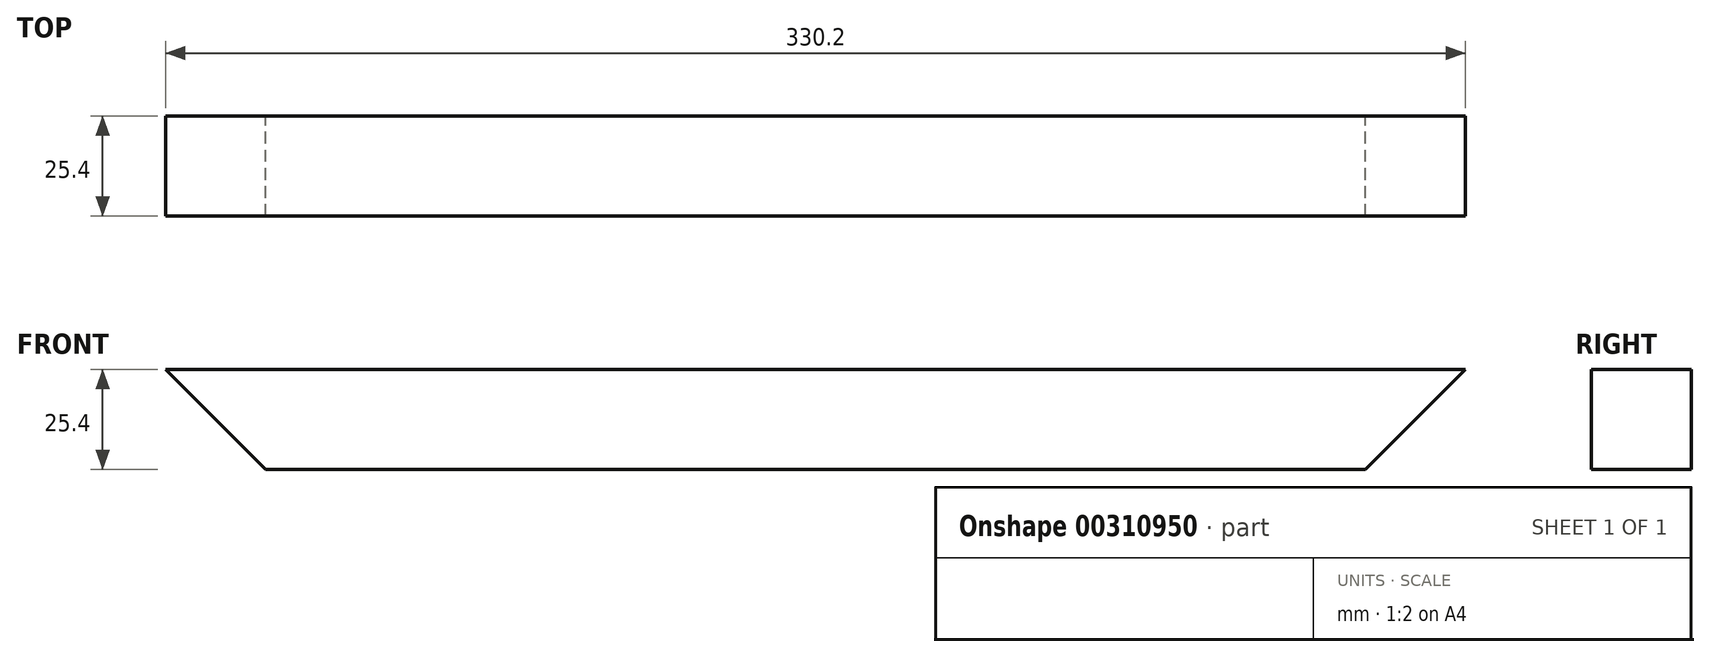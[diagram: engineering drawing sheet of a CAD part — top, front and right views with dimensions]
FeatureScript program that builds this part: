
annotation { "Feature Type Name" : "Feature", "Feature Type Description" : "" }
export const myFeature = defineFeature(function(context is Context, id is Id, definition is map)
    precondition{}
    {
        {
            var Q0;
            Q0=qCreatedBy(makeId("Front.planeOp"),FACE);
            var sketch = newSketch(context, id + "F0", { "sketchPlane" : qUnion([Q0])});
            skLineSegment(sketch, "E0.bottom", {"start": v(-87.22, 0) * mm, "end": v(192.18, 0) * mm});
            skLineSegment(sketch, "E0.top", {"start": v(-112.62, 25.4) * mm, "end": v(217.58, 25.4) * mm});
            skLineSegment(sketch, "E1", {"start": v(-112.62, 25.4) * mm, "end": v(-87.22, 0) * mm});
            skPoint(sketch, "E2.orphan", {"position": v(-93.8, 0) * mm});
            skLineSegment(sketch, "E3", {"start": v(217.58, 25.4) * mm, "end": v(192.18, 0) * mm});
            skSolve(sketch);
        }
        {
            var Q0;
            Q0 = qSketchRegion(id + "F0", true);
            extrude(context, id + "F1", {"entities" : qUnion([Q0]), "depth" : 25.4 * mm});
        }
    });
